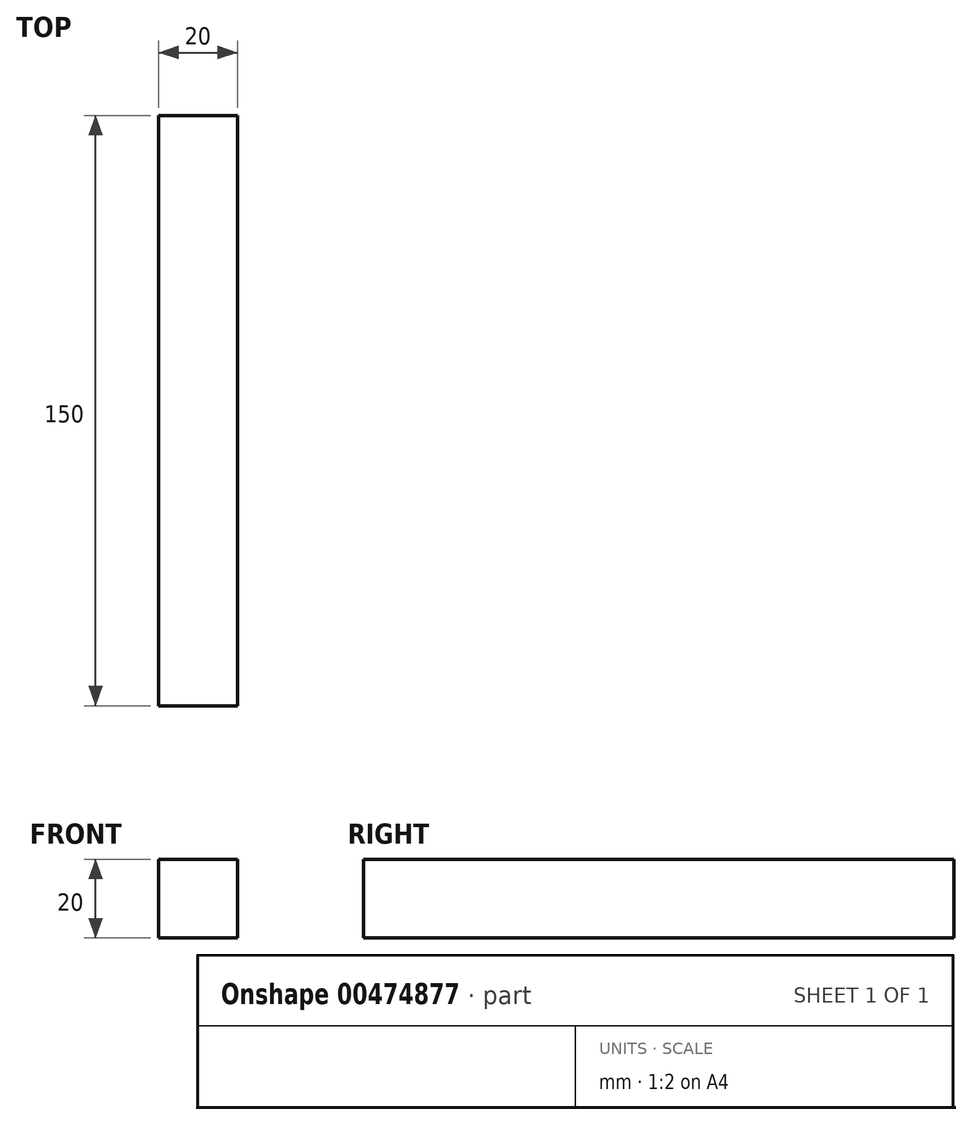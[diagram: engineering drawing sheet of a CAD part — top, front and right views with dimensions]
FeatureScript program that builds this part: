
annotation { "Feature Type Name" : "Feature", "Feature Type Description" : "" }
export const myFeature = defineFeature(function(context is Context, id is Id, definition is map)
    precondition{}
    {
        {
            var Q0;
            Q0=qCreatedBy(makeId("Front.planeOp"),FACE);
            var sketch = newSketch(context, id + "F0", { "sketchPlane" : qUnion([Q0])});
            skLineSegment(sketch, "E0.bottom", {"start": v(10, -10) * mm, "end": v(-10, -10) * mm});
            skLineSegment(sketch, "E0.top", {"start": v(10, 10) * mm, "end": v(-10, 10) * mm});
            skLineSegment(sketch, "E0.left", {"start": v(10, -10) * mm, "end": v(10, 10) * mm});
            skLineSegment(sketch, "E0.right", {"start": v(-10, -10) * mm, "end": v(-10, 10) * mm});
            skPoint(sketch, "E0.middle", {"position": v(0, 0) * mm});
            skSolve(sketch);
        }
        {
            var Q0;
            Q0=qSketchRegion(id+"F0",true);
            extrude(context, id + "F1", {"entities" : qUnion([Q0]), "endBound" : BoundingType.SYMMETRIC, "depth" : 150 * mm});
        }
    });
